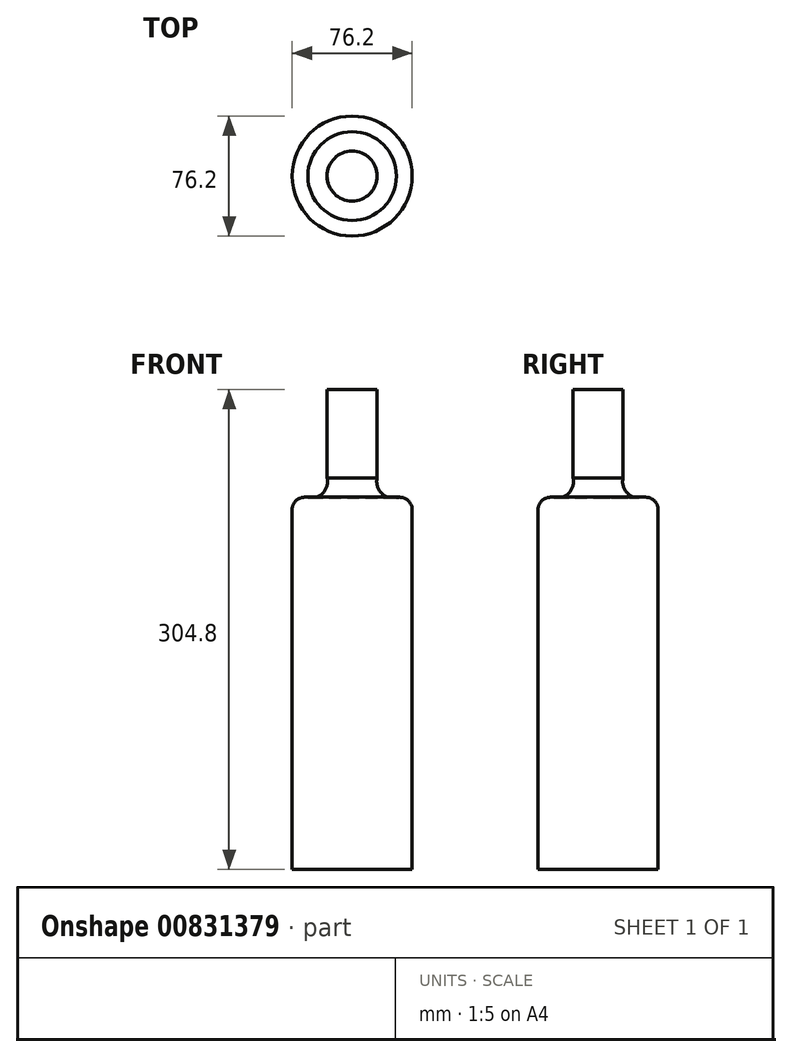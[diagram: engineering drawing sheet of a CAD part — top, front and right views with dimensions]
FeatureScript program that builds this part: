
annotation { "Feature Type Name" : "Feature", "Feature Type Description" : "" }
export const myFeature = defineFeature(function(context is Context, id is Id, definition is map)
    precondition{}
    {
        {
            var Q0;
            Q0=qCreatedBy(makeId("Front.planeOp"),FACE);
            var sketch = newSketch(context, id + "F0", { "sketchPlane" : qUnion([Q0])});
            skLineSegment(sketch, "E0", {"start": v(0, 48.03) * mm, "end": v(15.88, 48.03) * mm});
            skLineSegment(sketch, "E1", {"start": v(38.1, -28.17) * mm, "end": v(38.1, -256.77) * mm});
            skArc(sketch, "E2", {"start": v(15.88, -8.02) * mm, "mid": v(18.55, -17.7) * mm, "end": v(28.15, -20.66) * mm});
            skArc(sketch, "E3", {"start": v(38.1, -28.17) * mm, "mid": v(35, -21.94) * mm, "end": v(28.15, -20.66) * mm});
            skLineSegment(sketch, "E4", {"start": v(15.88, 48.03) * mm, "end": v(15.88, -8.02) * mm});
            skLineSegment(sketch, "E5", {"start": v(0, 48.03) * mm, "end": v(0, -256.77) * mm});
            skLineSegment(sketch, "E6", {"start": v(0, -256.77) * mm, "end": v(38.1, -256.77) * mm});
            skSolve(sketch);
        }
        {
            var Q0;
            Q0 = qSketchRegion(id + "F0", true);
            var Q1;
            Q1=sQuery(id+"F0.wireOp",EDGE,"E5");
            revolve(context, id + "F1", {"surfaceOperationType" : NewSurfaceOperationType.NEW, "entities" : qUnion([Q0]), "axis" : qUnion([Q1]), "revolveType" : RevolveType.FULL});
        }
    });
